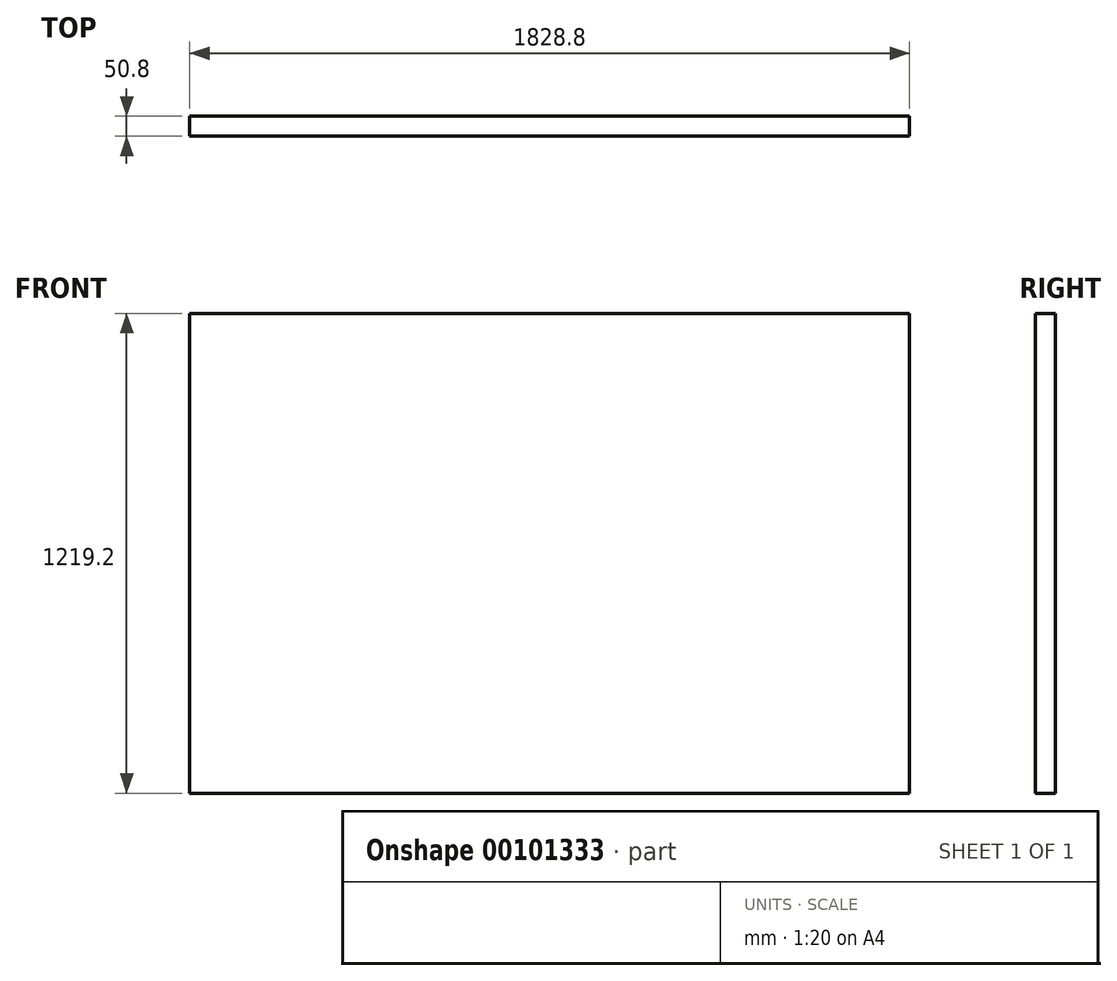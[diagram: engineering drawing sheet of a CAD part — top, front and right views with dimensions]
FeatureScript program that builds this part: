
annotation { "Feature Type Name" : "Feature", "Feature Type Description" : "" }
export const myFeature = defineFeature(function(context is Context, id is Id, definition is map)
    precondition{}
    {
        {
            var Q0;
            Q0=qCreatedBy(makeId("Front.planeOp"),FACE);
            var sketch = newSketch(context, id + "F0", { "sketchPlane" : qUnion([Q0])});
            skLineSegment(sketch, "E0.bottom", {"start": v(-914.4, 609.6) * mm, "end": v(914.4, 609.6) * mm});
            skLineSegment(sketch, "E0.top", {"start": v(-914.4, -609.6) * mm, "end": v(914.4, -609.6) * mm});
            skLineSegment(sketch, "E0.left", {"start": v(-914.4, 609.6) * mm, "end": v(-914.4, -609.6) * mm});
            skLineSegment(sketch, "E0.right", {"start": v(914.4, 609.6) * mm, "end": v(914.4, -609.6) * mm});
            skSolve(sketch);
        }
        {
            var Q0;
            Q0 = qSketchRegion(id + "F0", true);
            extrude(context, id + "F1", {"entities" : qUnion([Q0]), "endBound" : BoundingType.SYMMETRIC, "depth" : 50.8 * mm});
        }
    });
